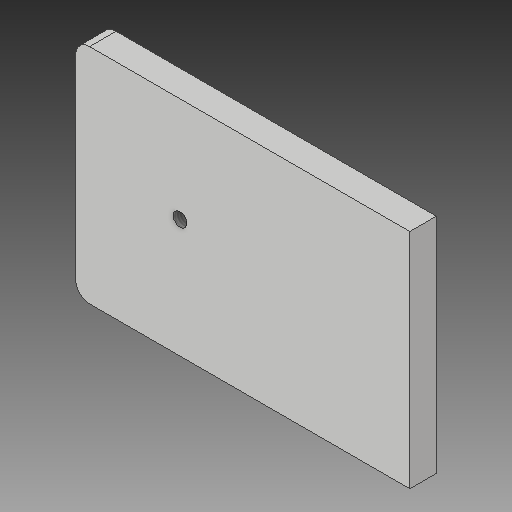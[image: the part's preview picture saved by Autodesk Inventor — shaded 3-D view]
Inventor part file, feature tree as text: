
AUTODESK INVENTOR PART (.ipt)
format: ipt  version: 2018 (Build 220112000, 112)  size: 89,600 bytes
history: native  units: mm
features: other x4, sketch x2
ambient origin geometry x8: Origin, YZ Plane, XZ Plane, XY Plane, X Axis, Y Axis, Z Axis, Center Point
bodies: Body1 (feature_tree)
feature tree (6):
  other  "SUPORTE_GUIA_CORREIA_EIXO_Y.ipt"
  other  "Sólido1::SUPORTE_GUIA_CORREIA_EIXO_Y.ipt"
  other  "OperaçãoIdentificador1"
  sketch  "Esboço1"  dims[d0=10.0mm]
  sketch  "Esboço11"
  other  "Sólido1"
